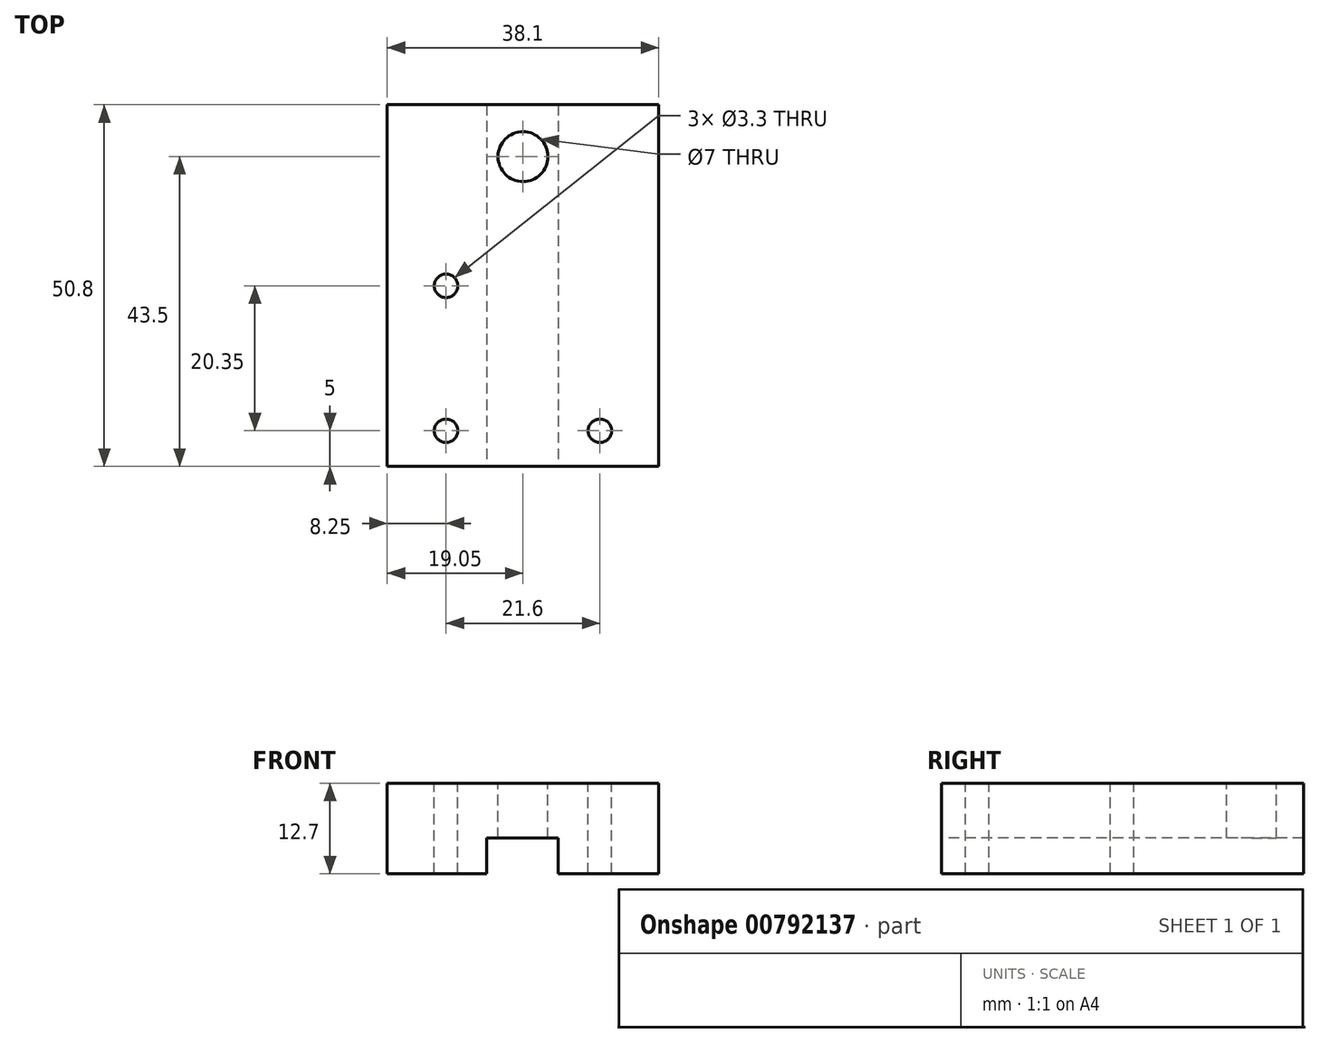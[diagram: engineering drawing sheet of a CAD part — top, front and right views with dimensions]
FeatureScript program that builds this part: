
annotation { "Feature Type Name" : "Feature", "Feature Type Description" : "" }
export const myFeature = defineFeature(function(context is Context, id is Id, definition is map)
    precondition{}
    {
        {
            var Q0;
            Q0=qCreatedBy(makeId("Top.planeOp"),FACE);
            var sketch = newSketch(context, id + "F0", { "sketchPlane" : qUnion([Q0])});
            skLineSegment(sketch, "E0.bottom", {"start": v(0, 0) * mm, "end": v(38.1, 0) * mm});
            skLineSegment(sketch, "E0.top", {"start": v(0, 50.8) * mm, "end": v(38.1, 50.8) * mm});
            skLineSegment(sketch, "E0.left", {"start": v(0, 0) * mm, "end": v(0, 50.8) * mm});
            skLineSegment(sketch, "E0.right", {"start": v(38.1, 0) * mm, "end": v(38.1, 50.8) * mm});
            skSolve(sketch);
        }
        {
            var Q0;
            Q0 = qSketchRegion(id + "F0", true);
            extrude(context, id + "F1", {"entities" : qUnion([Q0]), "depth" : 12.7 * mm, "offsetDistance" : 25.4 * mm});
        }
        {
            var Q0;
            Q0=makeQuery(id+"F1.opExtrude","CAP_FACE",FACE,{"disambiguationData":[OSD([sQuery(id+"F0.wireOp",EDGE,"E0.bottom"),sQuery(id+"F0.wireOp",EDGE,"E0.top"),sQuery(id+"F0.wireOp",EDGE,"E0.left"),sQuery(id+"F0.wireOp",EDGE,"E0.right")])],"isStart":false});
            var sketch = newSketch(context, id + "F2", { "sketchPlane" : qUnion([Q0])});
            skCircle(sketch, "E1", {"center": v(8.25, 5) * mm, "radius": 1.65 * mm});
            skCircle(sketch, "E2", {"center": v(29.85, 5) * mm, "radius": 1.65 * mm});
            skCircle(sketch, "E3", {"center": v(8.25, 25.35) * mm, "radius": 1.65 * mm});
            skLineSegment(sketch, "E4", {"start": v(0, 5) * mm, "end": v(8.25, 5) * mm, "construction": true});
            skLineSegment(sketch, "E5", {"start": v(29.85, 5) * mm, "end": v(38.1, 5) * mm, "construction": true});
            skCircle(sketch, "E6", {"center": v(19.05, 43.5) * mm, "radius": 3.5 * mm});
            skSolve(sketch);
        }
        {
            var Q0;
            Q0 = qSketchRegion(id + "F2", true);
            extrude(context, id + "F3", {"entities" : qUnion([Q0]), "operationType" : NewBodyOperationType.REMOVE, "endBound" : BoundingType.THROUGH_ALL, "oppositeDirection" : true, "depth" : 25 * mm, "offsetDistance" : 25 * mm});
        }
        {
            var Q0;
            Q0=makeQuery(id+"F1.opExtrude","SWEPT_FACE",FACE,{"disambiguationData":[OSD([sQuery(id+"F0.wireOp",EDGE,"E0.bottom")])]});
            var sketch = newSketch(context, id + "F4", { "sketchPlane" : qUnion([Q0])});
            skLineSegment(sketch, "E7.bottom", {"start": v(13.96, 0) * mm, "end": v(23.96, 0) * mm});
            skLineSegment(sketch, "E7.top", {"start": v(13.96, 5) * mm, "end": v(23.96, 5) * mm});
            skLineSegment(sketch, "E7.left", {"start": v(13.96, 0) * mm, "end": v(13.96, 5) * mm});
            skLineSegment(sketch, "E7.right", {"start": v(23.96, 0) * mm, "end": v(23.96, 5) * mm});
            skSolve(sketch);
        }
        {
            var Q0;
            Q0 = qSketchRegion(id + "F4", true);
            extrude(context, id + "F5", {"entities" : qUnion([Q0]), "operationType" : NewBodyOperationType.REMOVE, "endBound" : BoundingType.THROUGH_ALL, "oppositeDirection" : true, "depth" : 25 * mm, "offsetDistance" : 25 * mm});
        }
    });
